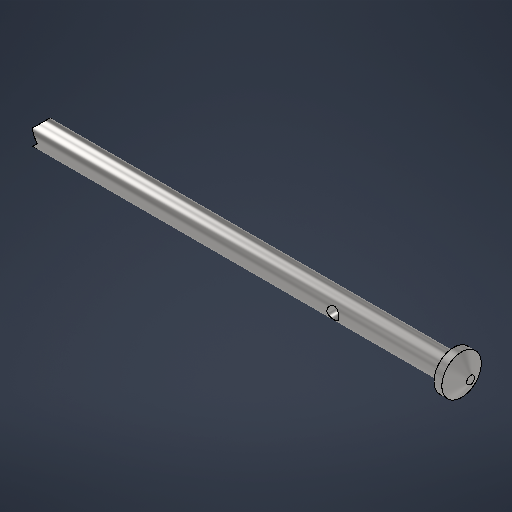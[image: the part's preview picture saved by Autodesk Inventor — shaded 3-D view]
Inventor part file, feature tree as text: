
AUTODESK INVENTOR PART (.ipt)
format: ipt  version: 2025.3 (Build 293356000, 356)  size: 236,032 bytes
history: native  units: mm
features: sketch x1, revolve x1, extrude x1
ambient origin geometry x8: Origin, YZ Plane, XZ Plane, XY Plane, X Axis, Y Axis, Z Axis, Center Point
bodies: Solid1 (feature_tree)
feature tree (3):
  sketch  "Sketch1"  dims[d0=6.0mm d2=60.0deg d3=2.0mm d4=10.0mm d5=2.0mm d6=110.0mm d7=360.0deg d8=0.0mm d9=0.0mm d10=3.0mm d14=2.0mm d16=32.0mm d13=0.872665mm]
  revolve  "Revolution1"  Angle=60.0deg
  extrude  "Extrusion1"  Depth=3.0mm
